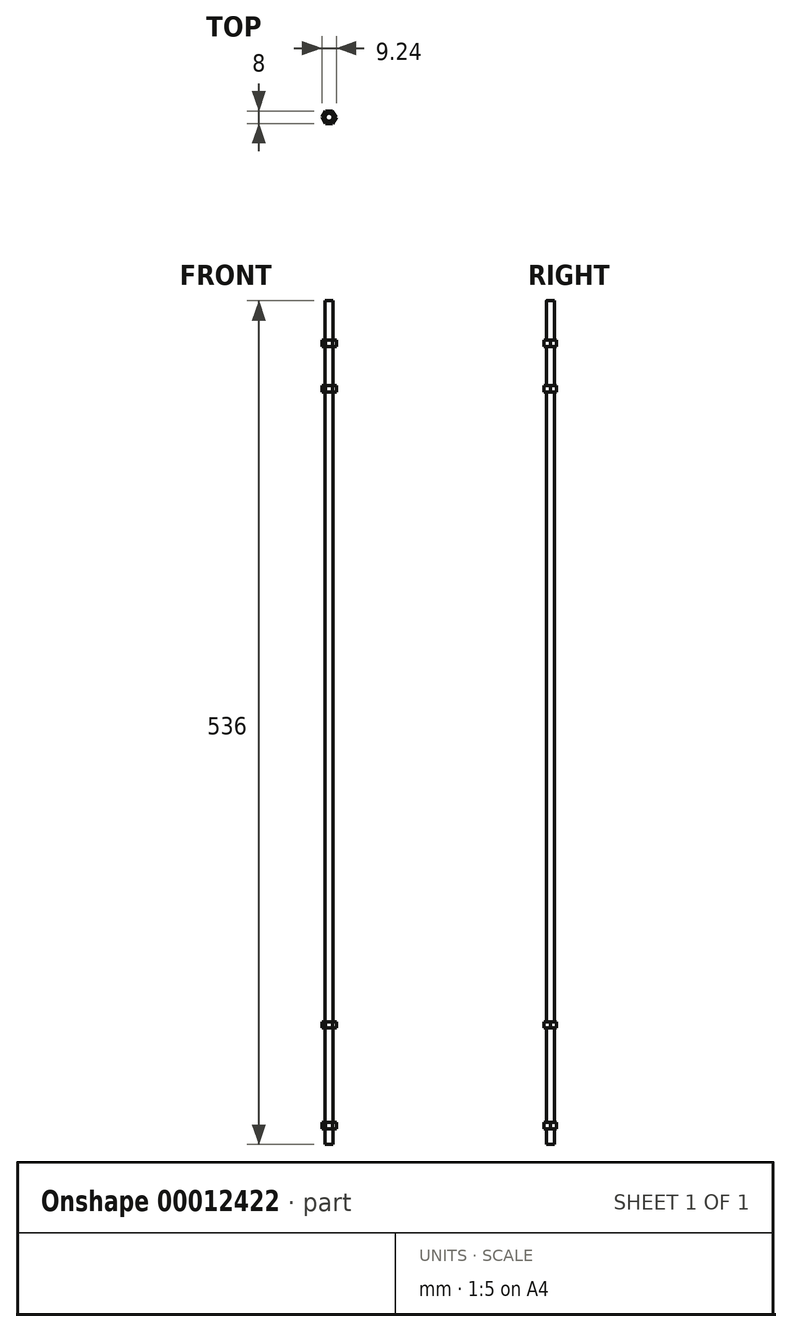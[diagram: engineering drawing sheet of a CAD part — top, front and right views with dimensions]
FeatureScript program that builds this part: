
annotation { "Feature Type Name" : "Feature", "Feature Type Description" : "" }
export const myFeature = defineFeature(function(context is Context, id is Id, definition is map)
    precondition{}
    {
        {
            var Q0;
            Q0=qCreatedBy(makeId("Top.planeOp"),FACE);
            var sketch = newSketch(context, id + "F0", { "sketchPlane" : qUnion([Q0])});
            skCircle(sketch, "E0", {"center": v(0, 0) * mm, "radius": 2.5 * mm});
            skSolve(sketch);
        }
        {
            var Q0;
            Q0 = qSketchRegion(id + "F0", true);
            extrude(context, id + "F1", {"entities" : qUnion([Q0]), "depth" : 400 * mm});
        }
        {
            var Q0;
            Q0=makeQuery(id+"F1.opExtrude","CAP_FACE",FACE,{"disambiguationData":[OSD([sQuery(id+"F0.wireOp",EDGE,"E0")])],"isStart":true});
            var sketch = newSketch(context, id + "F2", { "sketchPlane" : qUnion([Q0])});
            skCircle(sketch, "E1.cCircle", {"center": v(0, 0) * mm, "radius": 4 * mm, "construction": true});
            skLineSegment(sketch, "E1.0", {"start": v(-2.3, 4) * mm, "end": v(2.3, 4) * mm});
            skLineSegment(sketch, "E1.1", {"start": v(2.3, 4) * mm, "end": v(4.62, 0) * mm});
            skLineSegment(sketch, "E1.2", {"start": v(4.62, 0) * mm, "end": v(2.3, -4) * mm});
            skLineSegment(sketch, "E1.3", {"start": v(2.3, -4) * mm, "end": v(-2.3, -4) * mm});
            skLineSegment(sketch, "E1.4", {"start": v(-2.3, -4) * mm, "end": v(-4.62, 0) * mm});
            skLineSegment(sketch, "E1.5", {"start": v(-4.62, 0) * mm, "end": v(-2.3, 4) * mm});
            skPoint(sketch, "E1.0.midPoint", {"position": v(0, 4) * mm});
            skSolve(sketch);
        }
        {
            var Q0;
            Q0 = qSketchRegion(id + "F2", true);
            extrude(context, id + "F3", {"entities" : qUnion([Q0]), "operationType" : NewBodyOperationType.ADD, "depth" : 4 * mm});
        }
        {
            var Q0;
            Q0=makeQuery(id+"F3.opExtrude","CAP_FACE",FACE,{"disambiguationData":[OSD([sQuery(id+"F2.wireOp",EDGE,"E1.0"),sQuery(id+"F2.wireOp",EDGE,"E1.1"),sQuery(id+"F2.wireOp",EDGE,"E1.2"),sQuery(id+"F2.wireOp",EDGE,"E1.3"),sQuery(id+"F2.wireOp",EDGE,"E1.4"),sQuery(id+"F2.wireOp",EDGE,"E1.5")])],"isStart":false});
            var sketch = newSketch(context, id + "F4", { "sketchPlane" : qUnion([Q0])});
            skCircle(sketch, "E2.0", {"center": v(0, 0) * mm, "radius": 2.5 * mm});
            skSolve(sketch);
        }
        {
            var Q0;
            Q0 = qSketchRegion(id + "F4", true);
            extrude(context, id + "F5", {"entities" : qUnion([Q0]), "operationType" : NewBodyOperationType.ADD, "depth" : 60 * mm});
        }
        {
            var Q0;
            Q0=makeQuery(id+"F5.opExtrude","CAP_FACE",FACE,{"disambiguationData":[OSD([sQuery(id+"F4.wireOp",EDGE,"E2.0")])],"isStart":false});
            var sketch = newSketch(context, id + "F6", { "sketchPlane" : qUnion([Q0])});
            skLineSegment(sketch, "E3.0.0", {"start": v(2.3, 4) * mm, "end": v(-2.3, 4) * mm});
            skLineSegment(sketch, "E3.0.1", {"start": v(-2.3, 4) * mm, "end": v(-4.62, 0) * mm});
            skLineSegment(sketch, "E3.0.2", {"start": v(-4.62, 0) * mm, "end": v(-2.3, -4) * mm});
            skLineSegment(sketch, "E3.0.3", {"start": v(-2.3, -4) * mm, "end": v(2.3, -4) * mm});
            skLineSegment(sketch, "E3.0.4", {"start": v(2.3, -4) * mm, "end": v(4.62, 0) * mm});
            skLineSegment(sketch, "E3.0.5", {"start": v(4.62, 0) * mm, "end": v(2.3, 4) * mm});
            skSolve(sketch);
        }
        {
            var Q0;
            Q0 = qSketchRegion(id + "F6", true);
            extrude(context, id + "F7", {"entities" : qUnion([Q0]), "operationType" : NewBodyOperationType.ADD, "depth" : 4 * mm});
        }
        {
            var Q0;
            Q0=makeQuery(id+"F1.opExtrude","CAP_FACE",FACE,{"disambiguationData":[OSD([sQuery(id+"F0.wireOp",EDGE,"E0")])],"isStart":false});
            var sketch = newSketch(context, id + "F8", { "sketchPlane" : qUnion([Q0])});
            skLineSegment(sketch, "E4.0.0", {"start": v(-2.3, -4) * mm, "end": v(2.3, -4) * mm});
            skLineSegment(sketch, "E4.0.1", {"start": v(2.3, -4) * mm, "end": v(4.62, 0) * mm});
            skLineSegment(sketch, "E4.0.2", {"start": v(4.62, 0) * mm, "end": v(2.3, 4) * mm});
            skLineSegment(sketch, "E4.0.3", {"start": v(2.3, 4) * mm, "end": v(-2.3, 4) * mm});
            skLineSegment(sketch, "E4.0.4", {"start": v(-2.3, 4) * mm, "end": v(-4.62, 0) * mm});
            skLineSegment(sketch, "E4.0.5", {"start": v(-4.62, 0) * mm, "end": v(-2.3, -4) * mm});
            skSolve(sketch);
        }
        {
            var Q0;
            Q0 = qSketchRegion(id + "F8", true);
            extrude(context, id + "F9", {"entities" : qUnion([Q0]), "operationType" : NewBodyOperationType.ADD, "depth" : 4 * mm});
        }
        {
            var Q0;
            Q0=makeQuery(id+"F9.opExtrude","CAP_FACE",FACE,{"disambiguationData":[OSD([sQuery(id+"F8.wireOp",EDGE,"E4.0.0"),sQuery(id+"F8.wireOp",EDGE,"E4.0.1"),sQuery(id+"F8.wireOp",EDGE,"E4.0.2"),sQuery(id+"F8.wireOp",EDGE,"E4.0.3"),sQuery(id+"F8.wireOp",EDGE,"E4.0.4"),sQuery(id+"F8.wireOp",EDGE,"E4.0.5")])],"isStart":false});
            var sketch = newSketch(context, id + "F10", { "sketchPlane" : qUnion([Q0])});
            skCircle(sketch, "E5.0", {"center": v(0, 0) * mm, "radius": 2.5 * mm});
            skSolve(sketch);
        }
        {
            var Q0;
            Q0 = qSketchRegion(id + "F10", true);
            extrude(context, id + "F11", {"entities" : qUnion([Q0]), "operationType" : NewBodyOperationType.ADD, "depth" : 25 * mm});
        }
        {
            var Q0;
            Q0=makeQuery(id+"F11.opExtrude","CAP_FACE",FACE,{"disambiguationData":[OSD([sQuery(id+"F10.wireOp",EDGE,"E5.0")])],"isStart":false});
            var sketch = newSketch(context, id + "F12", { "sketchPlane" : qUnion([Q0])});
            skLineSegment(sketch, "E6.0.0", {"start": v(-4.62, 0) * mm, "end": v(-2.3, -4) * mm});
            skLineSegment(sketch, "E6.0.1", {"start": v(-2.3, -4) * mm, "end": v(2.3, -4) * mm});
            skLineSegment(sketch, "E6.0.2", {"start": v(2.3, -4) * mm, "end": v(4.62, 0) * mm});
            skLineSegment(sketch, "E6.0.3", {"start": v(4.62, 0) * mm, "end": v(2.3, 4) * mm});
            skLineSegment(sketch, "E6.0.4", {"start": v(2.3, 4) * mm, "end": v(-2.3, 4) * mm});
            skLineSegment(sketch, "E6.0.5", {"start": v(-2.3, 4) * mm, "end": v(-4.62, 0) * mm});
            skSolve(sketch);
        }
        {
            var Q0;
            Q0 = qSketchRegion(id + "F12", true);
            extrude(context, id + "F13", {"entities" : qUnion([Q0]), "operationType" : NewBodyOperationType.ADD, "depth" : 4 * mm});
        }
        {
            var Q0;
            Q0=makeQuery(id+"F13.opExtrude","CAP_FACE",FACE,{"disambiguationData":[OSD([sQuery(id+"F12.wireOp",EDGE,"E6.0.0"),sQuery(id+"F12.wireOp",EDGE,"E6.0.1"),sQuery(id+"F12.wireOp",EDGE,"E6.0.2"),sQuery(id+"F12.wireOp",EDGE,"E6.0.3"),sQuery(id+"F12.wireOp",EDGE,"E6.0.4"),sQuery(id+"F12.wireOp",EDGE,"E6.0.5")])],"isStart":false});
            var sketch = newSketch(context, id + "F14", { "sketchPlane" : qUnion([Q0])});
            skCircle(sketch, "E7.0", {"center": v(0, 0) * mm, "radius": 2.5 * mm});
            skSolve(sketch);
        }
        {
            var Q0;
            Q0 = qSketchRegion(id + "F14", true);
            extrude(context, id + "F15", {"entities" : qUnion([Q0]), "operationType" : NewBodyOperationType.ADD, "depth" : 25 * mm});
        }
        {
            var Q0;
            Q0=makeQuery(id+"F7.opExtrude","CAP_FACE",FACE,{"disambiguationData":[OSD([sQuery(id+"F6.wireOp",EDGE,"E3.0.0"),sQuery(id+"F6.wireOp",EDGE,"E3.0.1"),sQuery(id+"F6.wireOp",EDGE,"E3.0.2"),sQuery(id+"F6.wireOp",EDGE,"E3.0.3"),sQuery(id+"F6.wireOp",EDGE,"E3.0.4"),sQuery(id+"F6.wireOp",EDGE,"E3.0.5")])],"isStart":false});
            var sketch = newSketch(context, id + "F16", { "sketchPlane" : qUnion([Q0])});
            skCircle(sketch, "E8.0", {"center": v(0, 0) * mm, "radius": 2.5 * mm});
            skSolve(sketch);
        }
        {
            var Q0;
            Q0 = qSketchRegion(id + "F16", true);
            extrude(context, id + "F17", {"entities" : qUnion([Q0]), "operationType" : NewBodyOperationType.ADD, "depth" : 10 * mm});
        }
    });
